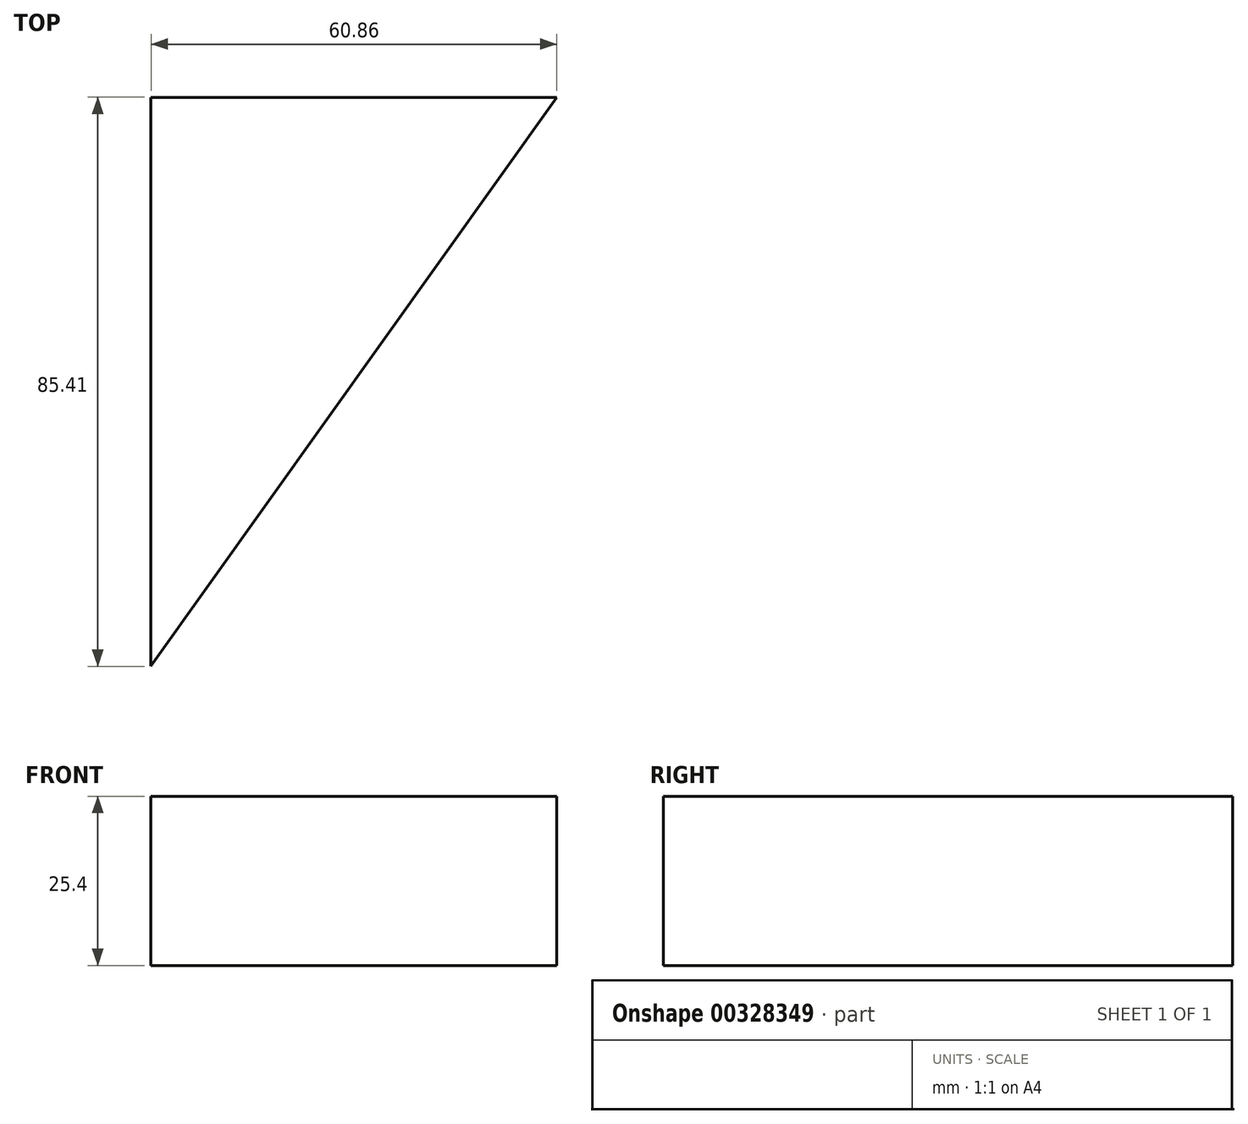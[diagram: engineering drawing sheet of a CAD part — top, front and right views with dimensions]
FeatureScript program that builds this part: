
annotation { "Feature Type Name" : "Feature", "Feature Type Description" : "" }
export const myFeature = defineFeature(function(context is Context, id is Id, definition is map)
    precondition{}
    {
        {
            var Q0;
            Q0=qCreatedBy(makeId("Top.planeOp"),FACE);
            var sketch = newSketch(context, id + "F0", { "sketchPlane" : qUnion([Q0])});
            skLineSegment(sketch, "E0", {"start": v(-21.24, -55.76) * mm, "end": v(-21.24, 29.65) * mm});
            skLineSegment(sketch, "E1", {"start": v(-21.24, 29.65) * mm, "end": v(39.62, 29.65) * mm});
            skLineSegment(sketch, "E2", {"start": v(39.62, 29.65) * mm, "end": v(-21.24, -55.76) * mm});
            skSolve(sketch);
        }
        {
            var Q0;
            Q0 = qSketchRegion(id + "F0", true);
            extrude(context, id + "F1", {"entities" : qUnion([Q0]), "depth" : 25.4 * mm});
        }
    });
